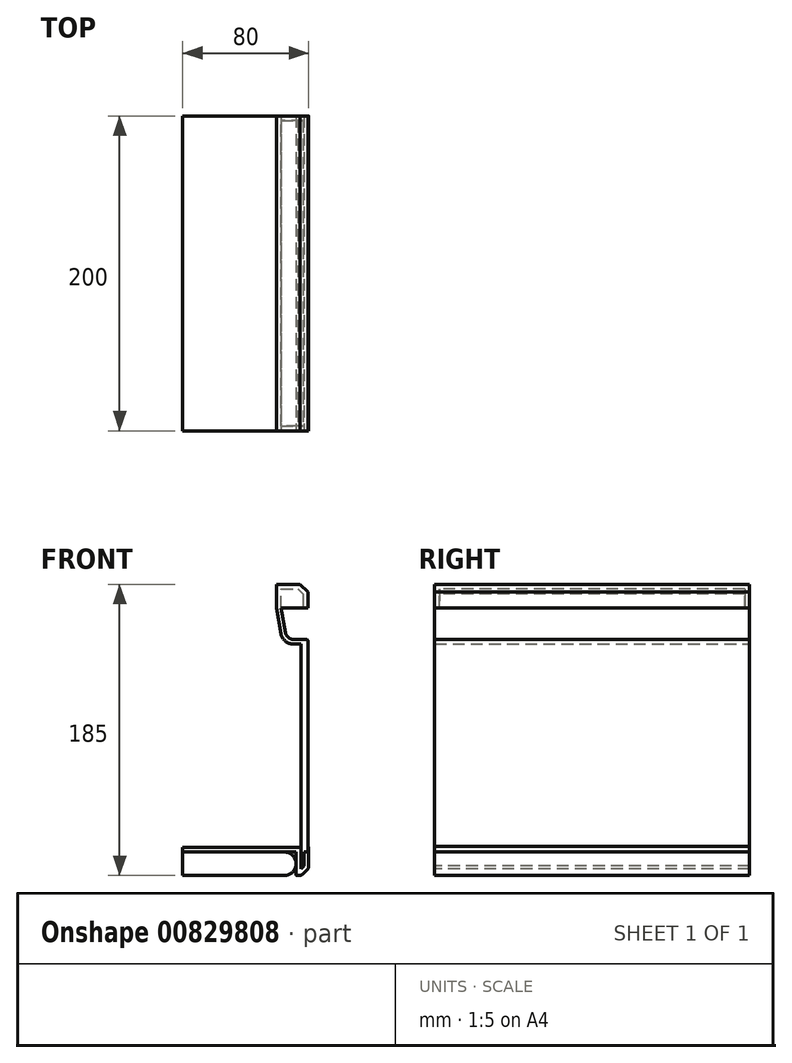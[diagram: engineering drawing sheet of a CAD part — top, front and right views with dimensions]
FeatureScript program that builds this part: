
annotation { "Feature Type Name" : "Feature", "Feature Type Description" : "" }
export const myFeature = defineFeature(function(context is Context, id is Id, definition is map)
    precondition{}
    {
        {
            var Q0;
            Q0=qCreatedBy(makeId("Front.planeOp"),FACE);
            var sketch = newSketch(context, id + "F0", { "sketchPlane" : qUnion([Q0])});
            skLineSegment(sketch, "E0", {"start": v(0, 0) * mm, "end": v(5, 5) * mm, "construction": true});
            skLineSegment(sketch, "E1", {"start": v(5, 5) * mm, "end": v(5, 15) * mm});
            skLineSegment(sketch, "E2", {"start": v(5, 15) * mm, "end": v(2, 15) * mm});
            skLineSegment(sketch, "E3", {"start": v(2, 15) * mm, "end": v(2, 6.24) * mm});
            skLineSegment(sketch, "E4", {"start": v(2, 6.24) * mm, "end": v(0, 4.24) * mm});
            skLineSegment(sketch, "E5", {"start": v(0, 4.24) * mm, "end": v(0, 18) * mm});
            skLineSegment(sketch, "E6", {"start": v(0, 18) * mm, "end": v(-75, 18) * mm});
            skLineSegment(sketch, "E7", {"start": v(-75, 18) * mm, "end": v(-75, 15) * mm});
            skLineSegment(sketch, "E8", {"start": v(-75, 15) * mm, "end": v(-3, 15) * mm});
            skLineSegment(sketch, "E9", {"start": v(-3, 15) * mm, "end": v(-3, 0) * mm});
            skLineSegment(sketch, "E10", {"start": v(0, 0) * mm, "end": v(-3, 0) * mm});
            skLineSegment(sketch, "E11", {"start": v(0, 15) * mm, "end": v(-3, 15) * mm, "construction": true});
            skLineSegment(sketch, "E12", {"start": v(2, 6.24) * mm, "end": v(4.12, 4.12) * mm, "construction": true});
            skArc(sketch, "E13", {"start": v(0, 0) * mm, "mid": v(2.71, 2.29) * mm, "end": v(5, 5) * mm});
            skLineSegment(sketch, "E14", {"start": v(2.5, 2.5) * mm, "end": v(2.71, 2.29) * mm, "construction": true});
            skSolve(sketch);
        }
        {
            var Q0;
            Q0=makeQuery(id+"F0.imprint","IMPRINT",FACE,{"disambiguationData":[TD([[makeQuery(id+"F0.imprint","IMPRINT",EDGE,{"derivedFrom":sQuery(id+"F0.wireOp",EDGE,"E1")}),1.0]])]});
            extrude(context, id + "F1", {"entities" : qUnion([Q0]), "oppositeDirection" : true, "depth" : 200 * mm, "offsetDistance" : 25.4 * mm});
        }
        {
            var Q0;
            Q0=makeQuery(id+"F1.opExtrude","CAP_FACE",FACE,{"disambiguationData":[OSD([sQuery(id+"F0.wireOp",EDGE,"E0"),sQuery(id+"F0.wireOp",EDGE,"E1"),sQuery(id+"F0.wireOp",EDGE,"E2"),sQuery(id+"F0.wireOp",EDGE,"E3"),sQuery(id+"F0.wireOp",EDGE,"E4"),sQuery(id+"F0.wireOp",EDGE,"E5"),sQuery(id+"F0.wireOp",EDGE,"E6"),sQuery(id+"F0.wireOp",EDGE,"E7"),sQuery(id+"F0.wireOp",EDGE,"E8"),sQuery(id+"F0.wireOp",EDGE,"E9"),sQuery(id+"F0.wireOp",EDGE,"E10")])],"isStart":true});
            var sketch = newSketch(context, id + "F2", { "sketchPlane" : qUnion([Q0])});
            skLineSegment(sketch, "E15", {"start": v(-75, 15) * mm, "end": v(-10.5, 15) * mm});
            skLineSegment(sketch, "E16", {"start": v(-10.5, 15) * mm, "end": v(-10.5, 0) * mm, "construction": true});
            skLineSegment(sketch, "E17", {"start": v(-10.5, 0) * mm, "end": v(-75, 0) * mm});
            skLineSegment(sketch, "E18", {"start": v(-75, 0) * mm, "end": v(-75, 15) * mm});
            skArc(sketch, "E19", {"start": v(-10.5, 0) * mm, "mid": v(-3, 7.5) * mm, "end": v(-10.5, 15) * mm});
            skSolve(sketch);
        }
        {
            var Q0;
            Q0 = qSketchRegion(id + "F2", true);
            var Q1;
            Q1=makeQuery(id+"F1.opExtrude","CAP_FACE",FACE,{"disambiguationData":[OSD([sQuery(id+"F0.wireOp",EDGE,"E0"),sQuery(id+"F0.wireOp",EDGE,"E1"),sQuery(id+"F0.wireOp",EDGE,"E2"),sQuery(id+"F0.wireOp",EDGE,"E3"),sQuery(id+"F0.wireOp",EDGE,"E4"),sQuery(id+"F0.wireOp",EDGE,"E5"),sQuery(id+"F0.wireOp",EDGE,"E6"),sQuery(id+"F0.wireOp",EDGE,"E7"),sQuery(id+"F0.wireOp",EDGE,"E8"),sQuery(id+"F0.wireOp",EDGE,"E9"),sQuery(id+"F0.wireOp",EDGE,"E10")])],"isStart":false});
            var Q2;
            Q2=makeQuery(id+"F1.opExtrude","CAP_FACE",FACE,{"disambiguationData":[OSD([sQuery(id+"F0.wireOp",EDGE,"E0"),sQuery(id+"F0.wireOp",EDGE,"E1"),sQuery(id+"F0.wireOp",EDGE,"E2"),sQuery(id+"F0.wireOp",EDGE,"E3"),sQuery(id+"F0.wireOp",EDGE,"E4"),sQuery(id+"F0.wireOp",EDGE,"E5"),sQuery(id+"F0.wireOp",EDGE,"E6"),sQuery(id+"F0.wireOp",EDGE,"E7"),sQuery(id+"F0.wireOp",EDGE,"E8"),sQuery(id+"F0.wireOp",EDGE,"E9"),sQuery(id+"F0.wireOp",EDGE,"E10")])],"isStart":false});
            extrude(context, id + "F3", {"entities" : qUnion([Q0, Q1]), "oppositeDirection" : true, "depth" : 200 * mm, "endBoundEntityFace" : qUnion([Q2]), "offsetDistance" : 25 * mm});
        }
        {
            var Q0;
            Q0=makeQuery(id+"F3.opExtrude","SWEPT_BODY",BODY,{"disambiguationData":[OSD([sQuery(id+"F0.wireOp",EDGE,"E0"),sQuery(id+"F0.wireOp",EDGE,"E1"),sQuery(id+"F0.wireOp",EDGE,"E2"),sQuery(id+"F0.wireOp",EDGE,"E3"),sQuery(id+"F0.wireOp",EDGE,"E4"),sQuery(id+"F0.wireOp",EDGE,"E5"),sQuery(id+"F0.wireOp",EDGE,"E6"),sQuery(id+"F0.wireOp",EDGE,"E7"),sQuery(id+"F0.wireOp",EDGE,"E8"),sQuery(id+"F0.wireOp",EDGE,"E9"),sQuery(id+"F0.wireOp",EDGE,"E10")])]});
            deleteBodies(context, id + "F4", {"entities" : qUnion([Q0])});
        }
        {
            var Q0;
            Q0=makeQuery(id+"F1.opExtrude","CAP_FACE",FACE,{"disambiguationData":[OSD([sQuery(id+"F0.wireOp",EDGE,"E0"),sQuery(id+"F0.wireOp",EDGE,"E1"),sQuery(id+"F0.wireOp",EDGE,"E2"),sQuery(id+"F0.wireOp",EDGE,"E3"),sQuery(id+"F0.wireOp",EDGE,"E4"),sQuery(id+"F0.wireOp",EDGE,"E5"),sQuery(id+"F0.wireOp",EDGE,"E6"),sQuery(id+"F0.wireOp",EDGE,"E7"),sQuery(id+"F0.wireOp",EDGE,"E8"),sQuery(id+"F0.wireOp",EDGE,"E9"),sQuery(id+"F0.wireOp",EDGE,"E10")])],"isStart":true});
            var sketch = newSketch(context, id + "F5", { "sketchPlane" : qUnion([Q0])});
            skLineSegment(sketch, "E20.0", {"start": v(0, 4.24) * mm, "end": v(0, 18) * mm});
            skLineSegment(sketch, "E21.0", {"start": v(2, 6.24) * mm, "end": v(0, 4.24) * mm});
            skLineSegment(sketch, "E22.0", {"start": v(2, 15) * mm, "end": v(2, 6.24) * mm});
            skLineSegment(sketch, "E23.0", {"start": v(5, 15) * mm, "end": v(2, 15) * mm, "construction": true});
            skPoint(sketch, "E24.0.end.orphan", {"position": v(-75, 18) * mm});
            skLineSegment(sketch, "E25", {"start": v(0, 18) * mm, "end": v(0, 150) * mm});
            skLineSegment(sketch, "E26", {"start": v(0, 150) * mm, "end": v(5, 150) * mm, "construction": true});
            skLineSegment(sketch, "E27", {"start": v(5, 150) * mm, "end": v(5, 15) * mm, "construction": true});
            skLineSegment(sketch, "E28", {"start": v(4.5, 15) * mm, "end": v(4.5, 150) * mm});
            skLineSegment(sketch, "E29", {"start": v(2, 15) * mm, "end": v(4.5, 15) * mm});
            skLineSegment(sketch, "E30", {"start": v(0, 150) * mm, "end": v(4.5, 150) * mm});
            skSolve(sketch);
        }
        {
            var Q0;
            Q0 = qSketchRegion(id + "F5", true);
            extrude(context, id + "F6", {"entities" : qUnion([Q0]), "oppositeDirection" : true, "depth" : 200 * mm, "offsetDistance" : 25 * mm});
        }
        {
            var Q0;
            Q0=makeQuery(id+"F1.opExtrude","SWEPT_EDGE",EDGE,{"disambiguationData":[OSD([sQuery(id+"F0.wireOp",EDGE,"E0"),sQuery(id+"F0.wireOp",EDGE,"E1")])]});
            var Q1;
            Q1=makeQuery(id+"F1.opExtrude","SWEPT_EDGE",EDGE,{"disambiguationData":[OSD([sQuery(id+"F0.wireOp",EDGE,"E0"),sQuery(id+"F0.wireOp",EDGE,"E10")])]});
            var Q2;
            Q2=makeQuery(id+"F1.opExtrude","SWEPT_EDGE",EDGE,{"disambiguationData":[OSD([sQuery(id+"F0.wireOp",EDGE,"E1"),sQuery(id+"F0.wireOp",EDGE,"E2")])]});
            fillet(context, id + "F7", {"entities" : qUnion([Q0, Q1, Q2]), "radius" : .5 * mm, "tangentPropagation" : true, "allowEdgeOverflow" : false});
        }
        {
            var Q0;
            Q0=makeQuery(id+"F5.imprint","IMPRINT",FACE,{"disambiguationData":[TD([[makeQuery(id+"F5.imprint","IMPRINT",EDGE,{"derivedFrom":sQuery(id+"F5.wireOp",EDGE,"E20.0")}),-1.0]])]});
            var sketch = newSketch(context, id + "F8", { "sketchPlane" : qUnion([Q0])});
            skLineSegment(sketch, "E31.bottom", {"start": v(5, 15) * mm, "end": v(4.5, 15) * mm});
            skLineSegment(sketch, "E31.top", {"start": v(5, 18.5) * mm, "end": v(4.5, 18.5) * mm});
            skLineSegment(sketch, "E31.left", {"start": v(5, 15) * mm, "end": v(5, 18.5) * mm});
            skLineSegment(sketch, "E31.right", {"start": v(4.5, 15) * mm, "end": v(4.5, 18.5) * mm});
            skSolve(sketch);
        }
        {
            var Q0;
            Q0 = qSketchRegion(id + "F8", true);
            var Q1;
            Q1 = qBodyType(qCreatedBy(id + "F8" ,EDGE), BodyType.WIRE);
            var Q2;
            Q2=sQuery(id+"F8.wireOp",EDGE,"E31.left");
            var Q3;
            Q3=makeQuery(id+"F6.opExtrude","CAP_FACE",FACE,{"disambiguationData":[OSD([sQuery(id+"F5.wireOp",EDGE,"E20.0"),sQuery(id+"F5.wireOp",EDGE,"E21.0"),sQuery(id+"F5.wireOp",EDGE,"E22.0"),sQuery(id+"F5.wireOp",EDGE,"E25"),sQuery(id+"F5.wireOp",EDGE,"E28"),sQuery(id+"F5.wireOp",EDGE,"E29"),sQuery(id+"F5.wireOp",EDGE,"E30")])],"isStart":false});
            extrude(context, id + "F9", {"entities" : qUnion([Q0]), "surfaceEntities" : qUnion([Q1, Q2]), "endBound" : BoundingType.UP_TO_SURFACE, "oppositeDirection" : true, "depth" : 25 * mm, "endBoundEntityFace" : qUnion([Q3]), "offsetDistance" : 25 * mm});
        }
        {
            var Q0;
            Q0=makeQuery(id+"F9.opExtrude","SWEPT_EDGE",EDGE,{"disambiguationData":[OSD([sQuery(id+"F8.wireOp",EDGE,"E31.top"),sQuery(id+"F8.wireOp",EDGE,"E31.left")])]});
            chamfer(context, id + "F10", {"entities" : qUnion([Q0]), "width" : .5 * mm, "tangentPropagation" : true});
        }
        {
            var Q0;
            {var subQ0=sQuery(id+"F8.wireOp",EDGE,"E31.left");Q0=makeQuery(id+"F10.opChamfer","BLEND_EDGE",EDGE,{"blendedFrom":[makeQuery(id+"F9.opExtrude","SWEPT_EDGE",EDGE,{"disambiguationData":[OSD([sQuery(id+"F8.wireOp",EDGE,"E31.top"),subQ0])]}),makeQuery(id+"F9.opExtrude","SWEPT_FACE",FACE,{"disambiguationData":[OSD([subQ0])]})],"blendedInto":[makeQuery(id+"F9.opExtrude","SWEPT_FACE",FACE,{"disambiguationData":[OSD([subQ0])]})]});}
            var Q1;
            Q1=makeQuery(id+"F9.opExtrude","SWEPT_EDGE",EDGE,{"disambiguationData":[OSD([sQuery(id+"F8.wireOp",EDGE,"E31.bottom"),sQuery(id+"F8.wireOp",EDGE,"E31.left")])]});
            fillet(context, id + "F11", {"entities" : qUnion([Q0, Q1]), "radius" : .5 * mm, "tangentPropagation" : true, "allowEdgeOverflow" : false});
        }
        {
            var Q0;
            Q0=makeQuery(id+"F6.opExtrude","CAP_FACE",FACE,{"disambiguationData":[OSD([sQuery(id+"F5.wireOp",EDGE,"E20.0"),sQuery(id+"F5.wireOp",EDGE,"E21.0"),sQuery(id+"F5.wireOp",EDGE,"E22.0"),sQuery(id+"F5.wireOp",EDGE,"E25"),sQuery(id+"F5.wireOp",EDGE,"E28"),sQuery(id+"F5.wireOp",EDGE,"E29"),sQuery(id+"F5.wireOp",EDGE,"E30")])],"isStart":true});
            var sketch = newSketch(context, id + "F12", { "sketchPlane" : qUnion([Q0])});
            skLineSegment(sketch, "E32", {"start": v(0, 150) * mm, "end": v(0, 170) * mm, "construction": true});
            skLineSegment(sketch, "E33", {"start": v(0, 170) * mm, "end": v(4.5, 170) * mm});
            skLineSegment(sketch, "E34", {"start": v(4.5, 170) * mm, "end": v(4.5, 150) * mm, "construction": true});
            skLineSegment(sketch, "E35", {"start": v(4.5, 170) * mm, "end": v(4.5, 180) * mm});
            skLineSegment(sketch, "E36", {"start": v(4.5, 180) * mm, "end": v(-0.5, 185) * mm});
            skLineSegment(sketch, "E37", {"start": v(-0.5, 185) * mm, "end": v(-15.5, 185) * mm});
            skLineSegment(sketch, "E38", {"start": v(-15.5, 185) * mm, "end": v(-15.5, 170) * mm});
            skLineSegment(sketch, "E39", {"start": v(-15.5, 170) * mm, "end": v(0, 170) * mm});
            skSolve(sketch);
        }
        {
            var Q0;
            Q0 = qSketchRegion(id + "F12", true);
            var Q1;
            Q1=makeQuery(id+"F6.opExtrude","CAP_FACE",FACE,{"disambiguationData":[OSD([sQuery(id+"F5.wireOp",EDGE,"E20.0"),sQuery(id+"F5.wireOp",EDGE,"E21.0"),sQuery(id+"F5.wireOp",EDGE,"E22.0"),sQuery(id+"F5.wireOp",EDGE,"E25"),sQuery(id+"F5.wireOp",EDGE,"E28"),sQuery(id+"F5.wireOp",EDGE,"E29"),sQuery(id+"F5.wireOp",EDGE,"E30")])],"isStart":false});
            extrude(context, id + "F13", {"entities" : qUnion([Q0]), "endBound" : BoundingType.UP_TO_SURFACE, "oppositeDirection" : true, "depth" : 25 * mm, "endBoundEntityFace" : qUnion([Q1]), "offsetDistance" : 25 * mm});
        }
        {
            var Q0;
            Q0=makeQuery(id+"F6.opExtrude","CAP_FACE",FACE,{"disambiguationData":[OSD([sQuery(id+"F5.wireOp",EDGE,"E20.0"),sQuery(id+"F5.wireOp",EDGE,"E21.0"),sQuery(id+"F5.wireOp",EDGE,"E22.0"),sQuery(id+"F5.wireOp",EDGE,"E25"),sQuery(id+"F5.wireOp",EDGE,"E28"),sQuery(id+"F5.wireOp",EDGE,"E29"),sQuery(id+"F5.wireOp",EDGE,"E30")])],"isStart":true});
            var sketch = newSketch(context, id + "F14", { "sketchPlane" : qUnion([Q0])});
            skLineSegment(sketch, "E40", {"start": v(4.5, 150) * mm, "end": v(-8.97, 150) * mm});
            skLineSegment(sketch, "E41", {"start": v(-8.97, 150) * mm, "end": v(-12.5, 170) * mm});
            skLineSegment(sketch, "E42", {"start": v(-12.5, 170) * mm, "end": v(-15.5, 170) * mm});
            skLineSegment(sketch, "E43", {"start": v(-15.5, 170) * mm, "end": v(-11.44, 147) * mm});
            skLineSegment(sketch, "E44", {"start": v(-11.44, 147) * mm, "end": v(4.5, 147) * mm});
            skLineSegment(sketch, "E45", {"start": v(4.5, 147) * mm, "end": v(4.5, 150) * mm});
            skSolve(sketch);
        }
        {
            var Q0;
            Q0 = qSketchRegion(id + "F14", true);
            var Q1;
            Q1=makeQuery(id+"F6.opExtrude","CAP_FACE",FACE,{"disambiguationData":[OSD([sQuery(id+"F5.wireOp",EDGE,"E20.0"),sQuery(id+"F5.wireOp",EDGE,"E21.0"),sQuery(id+"F5.wireOp",EDGE,"E22.0"),sQuery(id+"F5.wireOp",EDGE,"E25"),sQuery(id+"F5.wireOp",EDGE,"E28"),sQuery(id+"F5.wireOp",EDGE,"E29"),sQuery(id+"F5.wireOp",EDGE,"E30")])],"isStart":false});
            extrude(context, id + "F15", {"entities" : qUnion([Q0]), "operationType" : NewBodyOperationType.ADD, "endBound" : BoundingType.UP_TO_SURFACE, "oppositeDirection" : true, "depth" : 25 * mm, "endBoundEntityFace" : qUnion([Q1]), "offsetDistance" : 25 * mm});
        }
        {
            var Q0;
            Q0=makeQuery(id+"F15.opExtrude","SWEPT_EDGE",EDGE,{"disambiguationData":[OSD([sQuery(id+"F14.wireOp",EDGE,"E40"),sQuery(id+"F14.wireOp",EDGE,"E41")])]});
            fillet(context, id + "F16", {"entities" : qUnion([Q0]), "radius" : 5 * mm, "tangentPropagation" : true, "allowEdgeOverflow" : false});
        }
        {
            var Q0;
            Q0=makeQuery(id+"F15.opExtrude","SWEPT_EDGE",EDGE,{"disambiguationData":[OSD([sQuery(id+"F14.wireOp",EDGE,"E43"),sQuery(id+"F14.wireOp",EDGE,"E44")])]});
            fillet(context, id + "F17", {"entities" : qUnion([Q0]), "radius" : 8 * mm, "tangentPropagation" : true, "allowEdgeOverflow" : false});
        }
        {
            var Q0;
            Q0=makeQuery(id+"F13.opExtrude","SWEPT_FACE",FACE,{"disambiguationData":[OSD([sQuery(id+"F12.wireOp",EDGE,"E33"),sQuery(id+"F12.wireOp",EDGE,"E39")])]});
            shell(context, id + "F18", {"entities" : qUnion([Q0]), "thickness" : 3 * mm});
        }
        {
            var Q0;
            Q0=makeQuery(id+"F6.opExtrude","SWEPT_EDGE",EDGE,{"disambiguationData":[OSD([sQuery(id+"F5.wireOp",EDGE,"E28"),sQuery(id+"F5.wireOp",EDGE,"E30")])]});
            fillet(context, id + "F19", {"entities" : qUnion([Q0]), "radius" : 1 * mm, "tangentPropagation" : true, "allowEdgeOverflow" : false});
        }
    });
